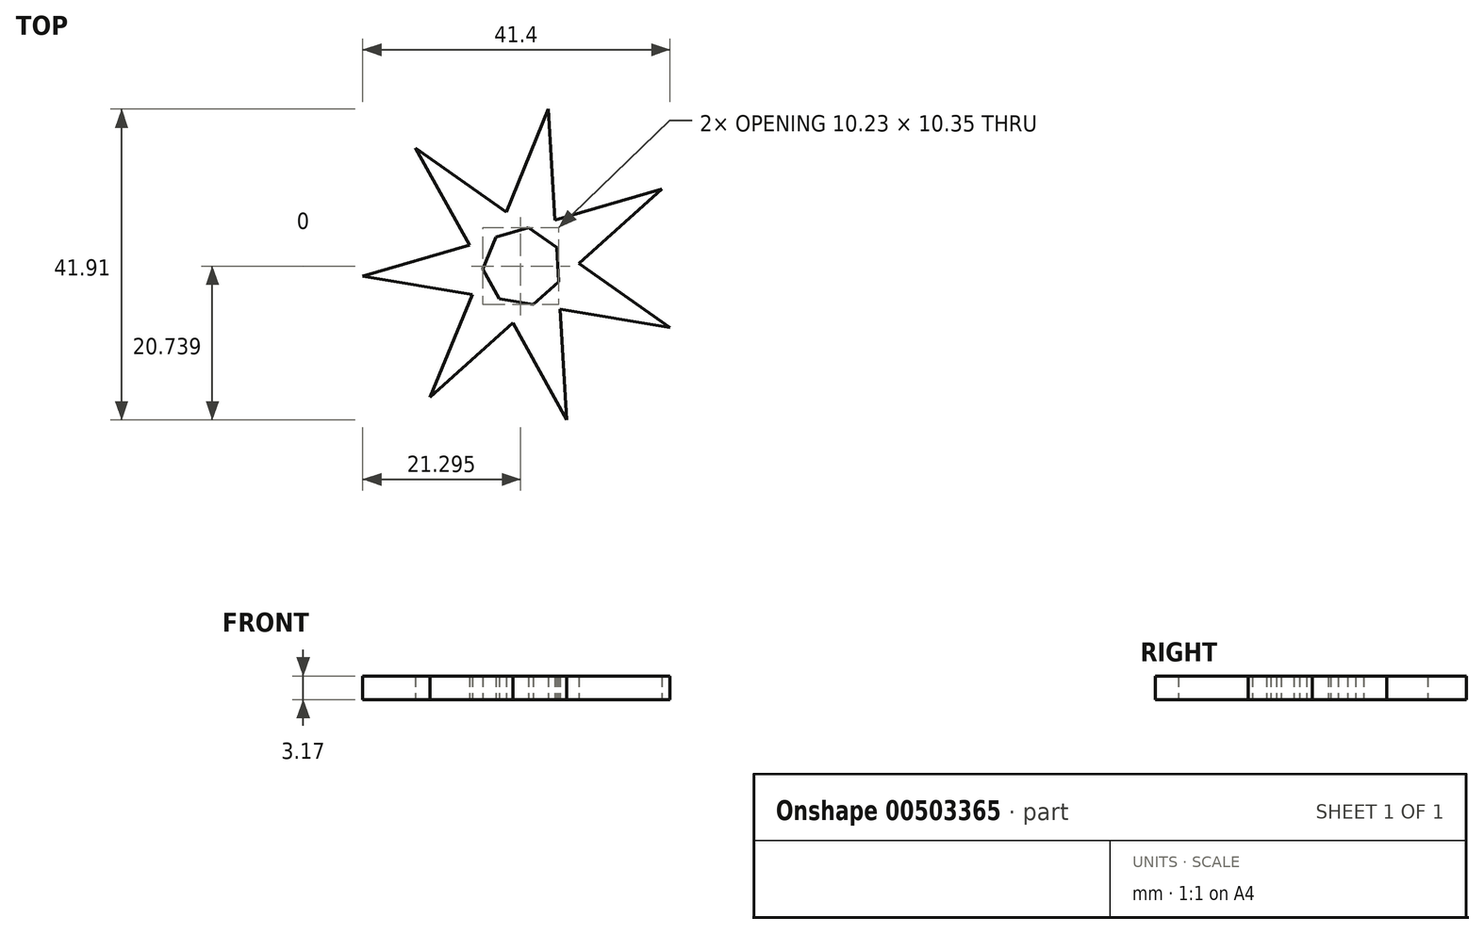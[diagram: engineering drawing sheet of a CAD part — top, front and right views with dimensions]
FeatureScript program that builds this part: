
annotation { "Feature Type Name" : "Feature", "Feature Type Description" : "" }
export const myFeature = defineFeature(function(context is Context, id is Id, definition is map)
    precondition{}
    {
        {
            var Q0;
            Q0=qCreatedBy(makeId("Top.planeOp"),FACE);
            var sketch = newSketch(context, id + "F0", { "sketchPlane" : qUnion([Q0])});
            skLineSegment(sketch, "E0.0", {"start": v(-21.5, -1.26) * mm, "end": v(-14.39, 16.02) * mm});
            skLineSegment(sketch, "E0.1", {"start": v(-14.39, 16.02) * mm, "end": v(3.55, 21.24) * mm});
            skLineSegment(sketch, "E0.2", {"start": v(3.55, 21.24) * mm, "end": v(18.82, 10.46) * mm});
            skLineSegment(sketch, "E0.3", {"start": v(18.82, 10.46) * mm, "end": v(19.91, -8.19) * mm});
            skLineSegment(sketch, "E0.4", {"start": v(19.91, -8.19) * mm, "end": v(6.01, -20.67) * mm});
            skLineSegment(sketch, "E0.5", {"start": v(6.01, -20.67) * mm, "end": v(-12.42, -17.6) * mm});
            skLineSegment(sketch, "E0.6", {"start": v(-12.42, -17.6) * mm, "end": v(-21.5, -1.26) * mm});
            skLineSegment(sketch, "E1", {"start": v(-12.42, -17.6) * mm, "end": v(3.55, 21.24) * mm});
            skLineSegment(sketch, "E2", {"start": v(3.55, 21.24) * mm, "end": v(6.01, -20.67) * mm});
            skLineSegment(sketch, "E3", {"start": v(6.01, -20.67) * mm, "end": v(-14.39, 16.02) * mm});
            skLineSegment(sketch, "E4", {"start": v(-14.39, 16.02) * mm, "end": v(19.91, -8.19) * mm});
            skLineSegment(sketch, "E5", {"start": v(19.91, -8.19) * mm, "end": v(-21.5, -1.26) * mm});
            skLineSegment(sketch, "E6", {"start": v(-21.5, -1.26) * mm, "end": v(18.82, 10.46) * mm});
            skLineSegment(sketch, "E7", {"start": v(18.82, 10.46) * mm, "end": v(-12.42, -17.6) * mm});
            skSolve(sketch);
        }
        {
            var Q0;
            {var subQ0=sQuery(id+"F0.wireOp",EDGE,"E7");var subQ5=sQuery(id+"F0.wireOp",EDGE,"E3");var subQ6=makeQuery(id+"F0.imprint","INTERSECT",VERTEX,{"derivedFrom":[subQ5,subQ0]});Q0=makeQuery(id+"F0.imprint","IMPRINT",FACE,{"disambiguationData":[TD([[makeQuery(id+"F0.imprint","IMPRINT",EDGE,{"disambiguationData":[TD([[subQ6,-1.0]])],"derivedFrom":subQ5}),1.0]])]});}
            var Q1;
            {var subQ1=sQuery(id+"F0.wireOp",EDGE,"E2");var subQ3=sQuery(id+"F0.wireOp",EDGE,"E5");var subQ4=makeQuery(id+"F0.imprint","INTERSECT",VERTEX,{"derivedFrom":[subQ1,subQ3]});Q1=makeQuery(id+"F0.imprint","IMPRINT",FACE,{"disambiguationData":[TD([[makeQuery(id+"F0.imprint","IMPRINT",EDGE,{"disambiguationData":[TD([[subQ4,-1.0]])],"derivedFrom":subQ3}),1.0]])]});}
            var Q2;
            {var subQ0=sQuery(id+"F0.wireOp",EDGE,"E7");var subQ1=sQuery(id+"F0.wireOp",EDGE,"E2");var subQ2=makeQuery(id+"F0.imprint","INTERSECT",VERTEX,{"derivedFrom":[subQ1,subQ0]});Q2=makeQuery(id+"F0.imprint","IMPRINT",FACE,{"disambiguationData":[TD([[makeQuery(id+"F0.imprint","IMPRINT",EDGE,{"disambiguationData":[TD([[subQ2,-1.0]])],"derivedFrom":subQ1}),1.0]])]});}
            var Q3;
            {var subQ0=sQuery(id+"F0.wireOp",EDGE,"E6");var subQ1=sQuery(id+"F0.wireOp",EDGE,"E2");var subQ2=makeQuery(id+"F0.imprint","INTERSECT",VERTEX,{"derivedFrom":[subQ1,subQ0]});Q3=makeQuery(id+"F0.imprint","IMPRINT",FACE,{"disambiguationData":[TD([[makeQuery(id+"F0.imprint","IMPRINT",EDGE,{"disambiguationData":[TD([[subQ2,-1.0]])],"derivedFrom":subQ1}),1.0]])]});}
            var Q4;
            {var subQ1=sQuery(id+"F0.wireOp",EDGE,"E1");var subQ3=sQuery(id+"F0.wireOp",EDGE,"E4");var subQ4=makeQuery(id+"F0.imprint","INTERSECT",VERTEX,{"derivedFrom":[subQ1,subQ3]});Q4=makeQuery(id+"F0.imprint","IMPRINT",FACE,{"disambiguationData":[TD([[makeQuery(id+"F0.imprint","IMPRINT",EDGE,{"disambiguationData":[TD([[subQ4,-1.0]])],"derivedFrom":subQ3}),1.0]])]});}
            var Q5;
            {var subQ0=sQuery(id+"F0.wireOp",EDGE,"E6");var subQ1=sQuery(id+"F0.wireOp",EDGE,"E1");var subQ2=makeQuery(id+"F0.imprint","INTERSECT",VERTEX,{"derivedFrom":[subQ1,subQ0]});Q5=makeQuery(id+"F0.imprint","IMPRINT",FACE,{"disambiguationData":[TD([[makeQuery(id+"F0.imprint","IMPRINT",EDGE,{"disambiguationData":[TD([[subQ2,-1.0]])],"derivedFrom":subQ1}),1.0]])]});}
            var Q6;
            {var subQ0=sQuery(id+"F0.wireOp",EDGE,"E5");var subQ1=sQuery(id+"F0.wireOp",EDGE,"E1");var subQ2=makeQuery(id+"F0.imprint","INTERSECT",VERTEX,{"derivedFrom":[subQ1,subQ0]});Q6=makeQuery(id+"F0.imprint","IMPRINT",FACE,{"disambiguationData":[TD([[makeQuery(id+"F0.imprint","IMPRINT",EDGE,{"disambiguationData":[TD([[subQ2,-1.0]])],"derivedFrom":subQ1}),1.0]])]});}
            var Q7;
            {var subQ0=sQuery(id+"F0.wireOp",EDGE,"E5");var subQ1=sQuery(id+"F0.wireOp",EDGE,"E1");var subQ2=makeQuery(id+"F0.imprint","INTERSECT",VERTEX,{"derivedFrom":[subQ1,subQ0]});Q7=makeQuery(id+"F0.imprint","IMPRINT",FACE,{"disambiguationData":[TD([[makeQuery(id+"F0.imprint","IMPRINT",EDGE,{"disambiguationData":[TD([[subQ2,-1.0]])],"derivedFrom":subQ1}),-1.0]])]});}
            var Q8;
            {var subQ0=sQuery(id+"F0.wireOp",EDGE,"E7");var subQ1=sQuery(id+"F0.wireOp",EDGE,"E2");var subQ2=makeQuery(id+"F0.imprint","INTERSECT",VERTEX,{"derivedFrom":[subQ1,subQ0]});Q8=makeQuery(id+"F0.imprint","IMPRINT",FACE,{"disambiguationData":[TD([[makeQuery(id+"F0.imprint","IMPRINT",EDGE,{"disambiguationData":[TD([[subQ2,-1.0]])],"derivedFrom":subQ1}),-1.0]])]});}
            var Q9;
            {var subQ0=sQuery(id+"F0.wireOp",EDGE,"E6");var subQ1=sQuery(id+"F0.wireOp",EDGE,"E2");var subQ2=makeQuery(id+"F0.imprint","INTERSECT",VERTEX,{"derivedFrom":[subQ1,subQ0]});Q9=makeQuery(id+"F0.imprint","IMPRINT",FACE,{"disambiguationData":[TD([[makeQuery(id+"F0.imprint","IMPRINT",EDGE,{"disambiguationData":[TD([[subQ2,-1.0]])],"derivedFrom":subQ1}),-1.0]])]});}
            var Q10;
            {var subQ0=sQuery(id+"F0.wireOp",EDGE,"E3");var subQ1=sQuery(id+"F0.wireOp",EDGE,"E1");var subQ2=makeQuery(id+"F0.imprint","INTERSECT",VERTEX,{"derivedFrom":[subQ1,subQ0]});Q10=makeQuery(id+"F0.imprint","IMPRINT",FACE,{"disambiguationData":[TD([[makeQuery(id+"F0.imprint","IMPRINT",EDGE,{"disambiguationData":[TD([[subQ2,-1.0]])],"derivedFrom":subQ1}),1.0]])]});}
            var Q11;
            {var subQ0=sQuery(id+"F0.wireOp",EDGE,"E7");var subQ1=sQuery(id+"F0.wireOp",EDGE,"E3");var subQ2=makeQuery(id+"F0.imprint","INTERSECT",VERTEX,{"derivedFrom":[subQ1,subQ0]});Q11=makeQuery(id+"F0.imprint","IMPRINT",FACE,{"disambiguationData":[TD([[makeQuery(id+"F0.imprint","IMPRINT",EDGE,{"disambiguationData":[TD([[subQ2,-1.0]])],"derivedFrom":subQ1}),-1.0]])]});}
            var Q12;
            {var subQ0=sQuery(id+"F0.wireOp",EDGE,"E4");var subQ1=sQuery(id+"F0.wireOp",EDGE,"E2");var subQ2=makeQuery(id+"F0.imprint","INTERSECT",VERTEX,{"derivedFrom":[subQ1,subQ0]});Q12=makeQuery(id+"F0.imprint","IMPRINT",FACE,{"disambiguationData":[TD([[makeQuery(id+"F0.imprint","IMPRINT",EDGE,{"disambiguationData":[TD([[subQ2,-1.0]])],"derivedFrom":subQ1}),1.0]])]});}
            var Q13;
            {var subQ0=sQuery(id+"F0.wireOp",EDGE,"E6");var subQ1=sQuery(id+"F0.wireOp",EDGE,"E1");var subQ2=makeQuery(id+"F0.imprint","INTERSECT",VERTEX,{"derivedFrom":[subQ1,subQ0]});Q13=makeQuery(id+"F0.imprint","IMPRINT",FACE,{"disambiguationData":[TD([[makeQuery(id+"F0.imprint","IMPRINT",EDGE,{"disambiguationData":[TD([[subQ2,-1.0]])],"derivedFrom":subQ1}),-1.0]])]});}
            extrude(context, id + "F1", {"entities" : qUnion([Q0, Q1, Q2, Q3, Q4, Q5, Q6, Q7, Q8, Q9, Q10, Q11, Q12, Q13]), "depth" : 3.17 * mm});
        }
    });
